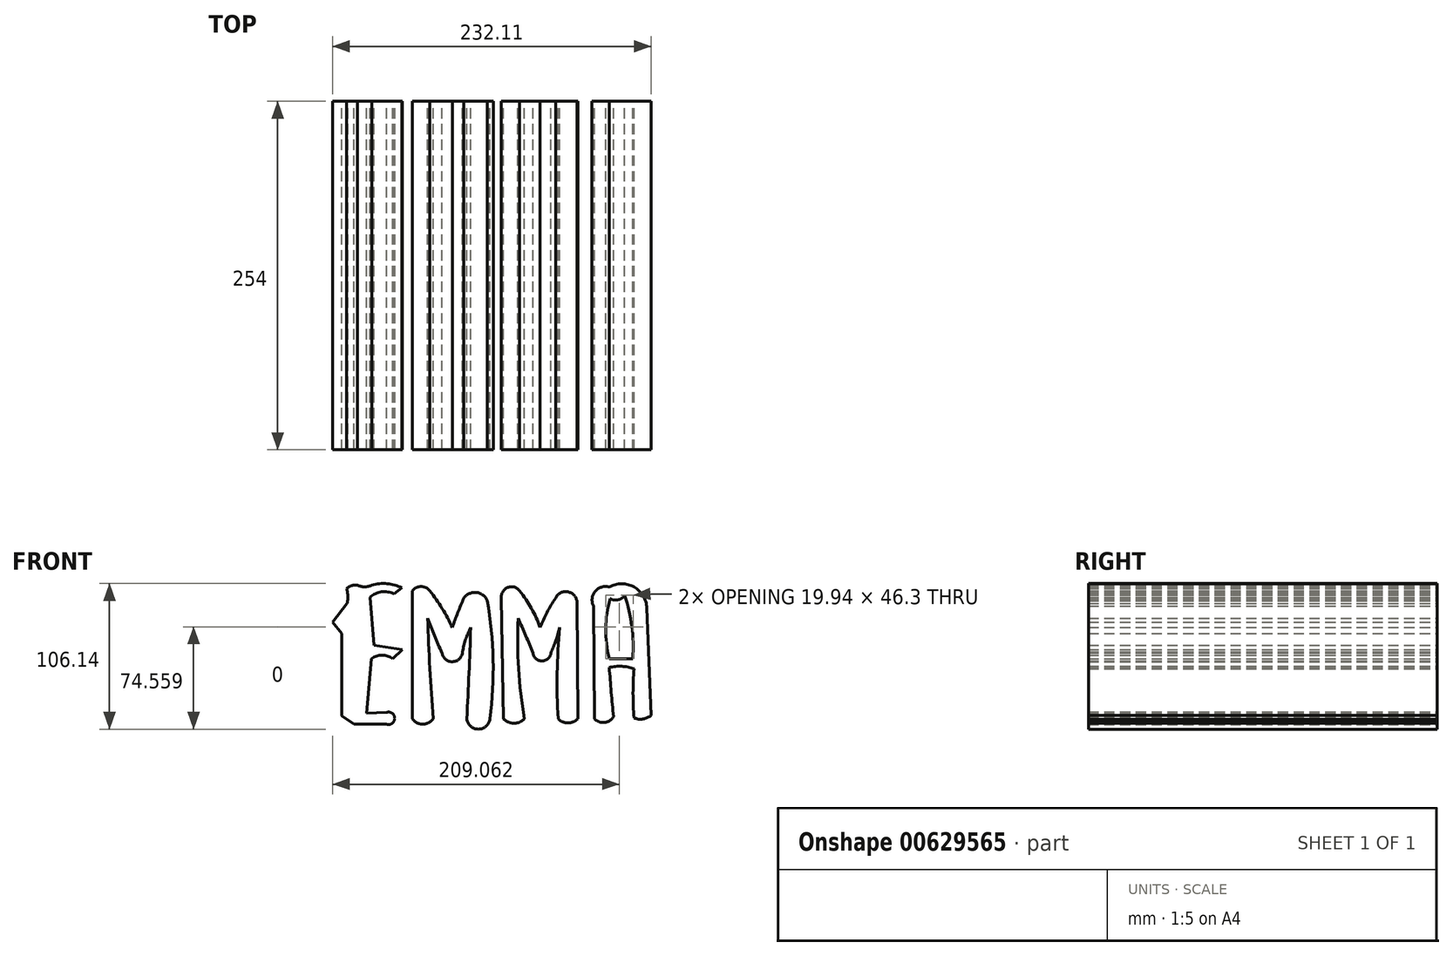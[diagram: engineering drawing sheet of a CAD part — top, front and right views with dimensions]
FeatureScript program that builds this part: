
annotation { "Feature Type Name" : "Feature", "Feature Type Description" : "" }
export const myFeature = defineFeature(function(context is Context, id is Id, definition is map)
    precondition{}
    {
        {
            var Q0;
            Q0=qCreatedBy(makeId("Front.planeOp"),FACE);
            var sketch = newSketch(context, id + "F0", { "sketchPlane" : qUnion([Q0])});
            skArc(sketch, "E0", {"start": v(-15.36, 51.58) * mm, "mid": v(-26.21, 54.62) * mm, "end": v(-37.42, 53.44) * mm});
            skArc(sketch, "E1", {"start": v(-47.98, 53.44) * mm, "mid": v(-42.7, 52.33) * mm, "end": v(-37.42, 53.44) * mm});
            skArc(sketch, "E2", {"start": v(-47.98, 53.44) * mm, "mid": v(-52.2, 53.25) * mm, "end": v(-55.75, 50.96) * mm});
            skArc(sketch, "E3", {"start": v(-55.44, 40.08) * mm, "mid": v(-54.83, 45.54) * mm, "end": v(-55.75, 50.96) * mm});
            skLineSegment(sketch, "E4", {"start": v(-66, 26.72) * mm, "end": v(-55.44, 40.08) * mm});
            skLineSegment(sketch, "E5", {"start": v(-66, 26.72) * mm, "end": v(-59.17, 18.33) * mm});
            skLineSegment(sketch, "E6", {"start": v(-59.17, 18.33) * mm, "end": v(-59.17, -41.64) * mm});
            skLineSegment(sketch, "E7", {"start": v(-59.17, -41.64) * mm, "end": v(-50.47, -47.85) * mm});
            skLineSegment(sketch, "E8", {"start": v(-50.47, -47.85) * mm, "end": v(-26.54, -47.85) * mm});
            skArc(sketch, "E9", {"start": v(-26.54, -47.85) * mm, "mid": v(-20.7, -43.5) * mm, "end": v(-26.54, -39.15) * mm});
            skLineSegment(sketch, "E10", {"start": v(-41.15, -39.77) * mm, "end": v(-26.54, -39.15) * mm});
            skLineSegment(sketch, "E11", {"start": v(-41.15, -39.77) * mm, "end": v(-37.73, 0) * mm});
            skArc(sketch, "E12", {"start": v(-22.2, 0) * mm, "mid": v(-29.96, 2.5) * mm, "end": v(-37.73, 0) * mm});
            skLineSegment(sketch, "E13", {"start": v(-22.2, 0) * mm, "end": v(-15.05, 6.53) * mm});
            skLineSegment(sketch, "E14", {"start": v(-15.05, 6.53) * mm, "end": v(-35.87, 9.63) * mm});
            skLineSegment(sketch, "E15", {"start": v(-35.87, 9.63) * mm, "end": v(-38.66, 44.74) * mm});
            skArc(sketch, "E16", {"start": v(-21.26, 47.23) * mm, "mid": v(-30.34, 48.64) * mm, "end": v(-38.66, 44.74) * mm});
            skLineSegment(sketch, "E17", {"start": v(-21.26, 47.23) * mm, "end": v(-15.36, 51.58) * mm});
            skLineSegment(sketch, "E18", {"start": v(-7.9, 49.4) * mm, "end": v(-7.9, -43.81) * mm});
            skPoint(sketch, "E18.startSnap0", {"position": v(-18.31, 49.4) * mm});
            skArc(sketch, "E19", {"start": v(-7.9, -43.81) * mm, "mid": v(-0.29, -47.76) * mm, "end": v(7.32, -43.81) * mm});
            skArc(sketch, "E20", {"start": v(4.84, 49.4) * mm, "mid": v(-1.53, 52.52) * mm, "end": v(-7.9, 49.4) * mm});
            skArc(sketch, "E21", {"start": v(13.85, 4.04) * mm, "mid": v(21.73, -2.23) * mm, "end": v(28.76, 4.97) * mm});
            skArc(sketch, "E22", {"start": v(46.79, 42.26) * mm, "mid": v(38.8, 48.24) * mm, "end": v(29.7, 44.12) * mm});
            skArc(sketch, "E23", {"start": v(31.87, -43.81) * mm, "mid": v(40.26, -51.41) * mm, "end": v(48.65, -43.81) * mm});
            skArc(sketch, "E24", {"start": v(3.28, 29.52) * mm, "mid": v(8.25, 16.65) * mm, "end": v(13.85, 4.04) * mm});
            skArc(sketch, "E25", {"start": v(34.67, 22.68) * mm, "mid": v(31.04, 14.05) * mm, "end": v(28.76, 4.97) * mm});
            skArc(sketch, "E26", {"start": v(3.28, 29.52) * mm, "mid": v(4.92, -7.17) * mm, "end": v(7.32, -43.81) * mm});
            skArc(sketch, "E27", {"start": v(31.87, -43.81) * mm, "mid": v(33.45, -10.57) * mm, "end": v(34.67, 22.68) * mm});
            skArc(sketch, "E28", {"start": v(48.65, -43.81) * mm, "mid": v(51, -0.7) * mm, "end": v(46.79, 42.26) * mm});
            skArc(sketch, "E29", {"start": v(21.26, 22.68) * mm, "mid": v(13.85, 36.53) * mm, "end": v(4.84, 49.4) * mm});
            skArc(sketch, "E30", {"start": v(29.7, 44.12) * mm, "mid": v(25.26, 33.49) * mm, "end": v(21.26, 22.68) * mm});
            skArc(sketch, "E31", {"start": v(80.03, 4.04) * mm, "mid": v(86.56, -1.71) * mm, "end": v(93.08, 4.04) * mm});
            skArc(sketch, "E32", {"start": v(70.4, 49.4) * mm, "mid": v(61.7, 51.89) * mm, "end": v(57.04, 44.12) * mm});
            skArc(sketch, "E33", {"start": v(112.04, 42.26) * mm, "mid": v(104.94, 48.78) * mm, "end": v(96.5, 44.12) * mm});
            skArc(sketch, "E34", {"start": v(69.16, 29.52) * mm, "mid": v(69.59, -7.27) * mm, "end": v(73.82, -43.81) * mm});
            skArc(sketch, "E35", {"start": v(99.6, 22.68) * mm, "mid": v(97.66, -10.54) * mm, "end": v(98.36, -43.81) * mm});
            skArc(sketch, "E36", {"start": v(80.03, 4.04) * mm, "mid": v(74.8, 16.87) * mm, "end": v(69.16, 29.52) * mm});
            skArc(sketch, "E37", {"start": v(93.08, 4.04) * mm, "mid": v(96.73, 13.23) * mm, "end": v(99.6, 22.68) * mm});
            skArc(sketch, "E38", {"start": v(85.31, 22.68) * mm, "mid": v(78.92, 36.64) * mm, "end": v(70.4, 49.4) * mm});
            skArc(sketch, "E39", {"start": v(96.5, 44.12) * mm, "mid": v(90.34, 33.7) * mm, "end": v(85.31, 22.68) * mm});
            skArc(sketch, "E40", {"start": v(58.6, -43.81) * mm, "mid": v(66.2, -47.12) * mm, "end": v(73.82, -43.81) * mm});
            skArc(sketch, "E41", {"start": v(98.36, -43.81) * mm, "mid": v(105.51, -46.85) * mm, "end": v(112.66, -43.81) * mm});
            skLineSegment(sketch, "E42", {"start": v(58.6, -43.81) * mm, "end": v(57.04, 44.12) * mm});
            skLineSegment(sketch, "E43", {"start": v(112.04, 42.26) * mm, "end": v(112.66, -43.81) * mm});
            skLineSegment(sketch, "E44", {"start": v(124.78, -43.81) * mm, "end": v(124.18, 38.23) * mm});
            skLineSegment(sketch, "E45", {"start": v(135.65, 0) * mm, "end": v(152.74, 0) * mm});
            skLineSegment(sketch, "E46", {"start": v(166.1, -41.33) * mm, "end": v(163, 36.91) * mm});
            skArc(sketch, "E47", {"start": v(153.67, -7.46) * mm, "mid": v(144.73, -5.59) * mm, "end": v(135.65, -6.53) * mm});
            skArc(sketch, "E48", {"start": v(136.27, 43.81) * mm, "mid": v(142.07, 42.85) * mm, "end": v(146.84, 46.3) * mm});
            skArc(sketch, "E49", {"start": v(136.27, 43.81) * mm, "mid": v(133.08, 21.95) * mm, "end": v(135.65, 0) * mm});
            skArc(sketch, "E50", {"start": v(152.74, 0) * mm, "mid": v(152.1, 23.44) * mm, "end": v(146.84, 46.3) * mm});
            skArc(sketch, "E51", {"start": v(135.65, -6.53) * mm, "mid": v(137.1, -24.4) * mm, "end": v(138.76, -42.26) * mm});
            skArc(sketch, "E52", {"start": v(153.67, -7.46) * mm, "mid": v(152.96, -25.32) * mm, "end": v(153.67, -43.19) * mm});
            skArc(sketch, "E53", {"start": v(153.67, -43.19) * mm, "mid": v(160.16, -44.05) * mm, "end": v(166.1, -41.33) * mm});
            skArc(sketch, "E54", {"start": v(124.78, -43.81) * mm, "mid": v(132.16, -46.56) * mm, "end": v(138.76, -42.26) * mm});
            skArc(sketch, "E55", {"start": v(135.65, 52.2) * mm, "mid": v(125.34, 48.97) * mm, "end": v(124.18, 38.23) * mm});
            skArc(sketch, "E56", {"start": v(163, 36.91) * mm, "mid": v(153.6, 52.21) * mm, "end": v(135.65, 52.2) * mm});
            skSolve(sketch);
        }
        {
            var Q0;
            Q0=makeQuery(id+"F0.imprint","IMPRINT",FACE,{"disambiguationData":[TD([[makeQuery(id+"F0.imprint","IMPRINT",EDGE,{"derivedFrom":sQuery(id+"F0.wireOp",EDGE,"E0")}),1.0]])]});
            var Q1;
            Q1=makeQuery(id+"F0.imprint","IMPRINT",FACE,{"disambiguationData":[TD([[makeQuery(id+"F0.imprint","IMPRINT",EDGE,{"derivedFrom":sQuery(id+"F0.wireOp",EDGE,"E18")}),1.0]])]});
            var Q2;
            Q2=makeQuery(id+"F0.imprint","IMPRINT",FACE,{"disambiguationData":[TD([[makeQuery(id+"F0.imprint","IMPRINT",EDGE,{"derivedFrom":sQuery(id+"F0.wireOp",EDGE,"E31")}),1.0]])]});
            var Q3;
            Q3=makeQuery(id+"F0.imprint","IMPRINT",FACE,{"disambiguationData":[TD([[makeQuery(id+"F0.imprint","IMPRINT",EDGE,{"derivedFrom":sQuery(id+"F0.wireOp",EDGE,"E44")}),-1.0]])]});
            extrude(context, id + "F1", {"entities" : qUnion([Q0, Q1, Q2, Q3]), "depth" : 254 * mm, "offsetDistance" : 25.4 * mm, "symmetric" : true});
        }
    });
